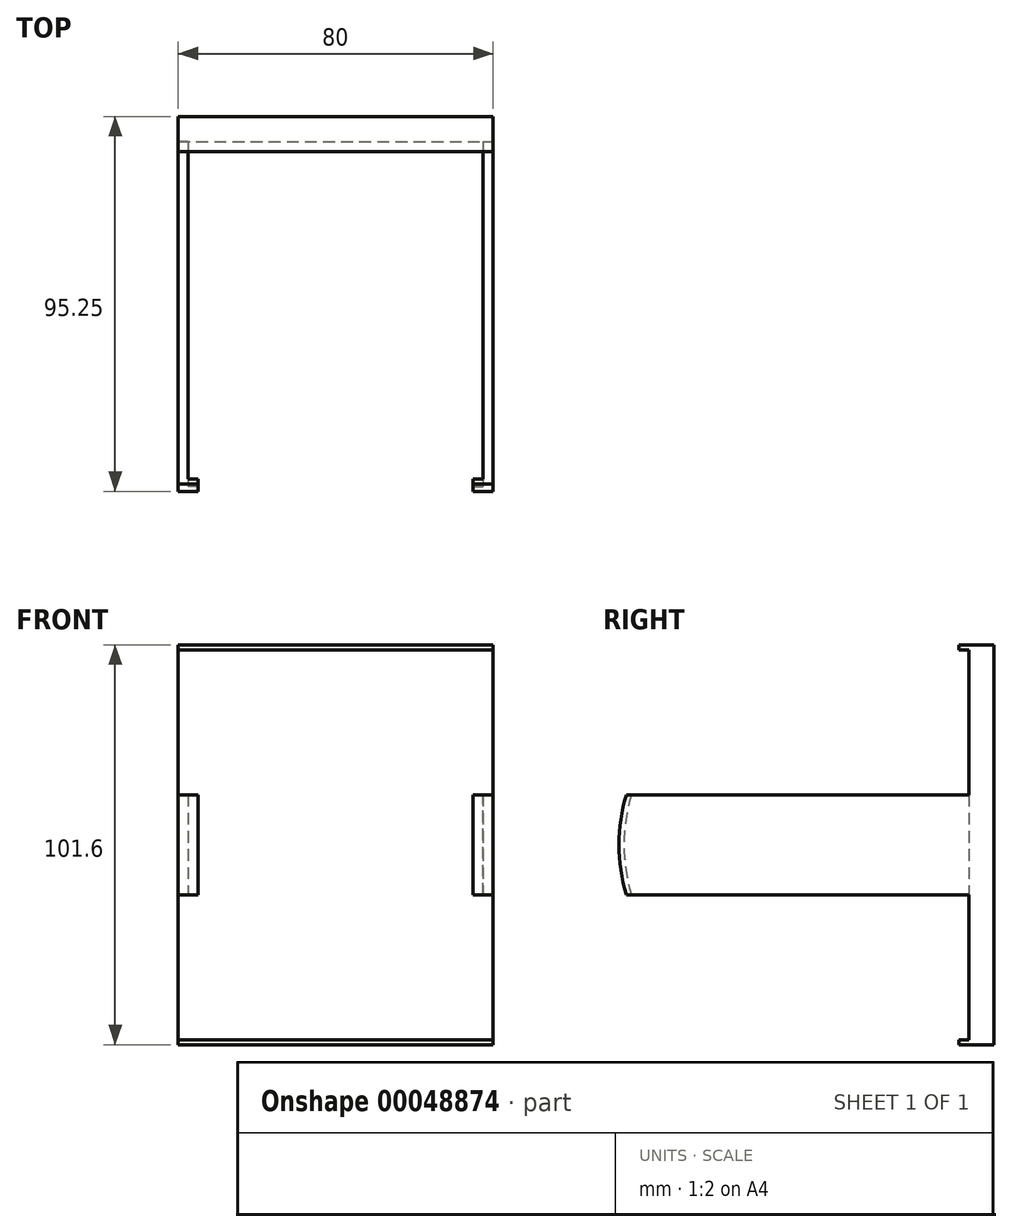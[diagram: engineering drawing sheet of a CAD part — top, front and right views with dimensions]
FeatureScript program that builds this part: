
annotation { "Feature Type Name" : "Feature", "Feature Type Description" : "" }
export const myFeature = defineFeature(function(context is Context, id is Id, definition is map)
    precondition{}
    {
        {
            var Q0;
            Q0=qCreatedBy(makeId("Front.planeOp"),FACE);
            var sketch = newSketch(context, id + "F0", { "sketchPlane" : qUnion([Q0])});
            skLineSegment(sketch, "E0.bottom", {"start": v(-21.88, 20.93) * mm, "end": v(58.12, 20.93) * mm});
            skLineSegment(sketch, "E0.top", {"start": v(-21.88, -80.67) * mm, "end": v(58.12, -80.67) * mm});
            skLineSegment(sketch, "E0.left", {"start": v(-21.88, 20.93) * mm, "end": v(-21.88, -80.67) * mm});
            skLineSegment(sketch, "E0.right", {"start": v(58.12, 20.93) * mm, "end": v(58.12, -80.67) * mm});
            skSolve(sketch);
        }
        {
            var Q0;
            Q0=makeQuery(id+"F0.imprint","IMPRINT",FACE,{"disambiguationData":[TD([[makeQuery(id+"F0.imprint","IMPRINT",EDGE,{"derivedFrom":sQuery(id+"F0.wireOp",EDGE,"E0.bottom")}),-1.0]])]});
            extrude(context, id + "F1", {"entities" : qUnion([Q0]), "depth" : 6.35 * mm});
        }
        {
            var Q0;
            Q0=makeQuery(id+"F1.opExtrude","SWEPT_FACE",FACE,{"disambiguationData":[OSD([sQuery(id+"F0.wireOp",EDGE,"E0.right")])]});
            var sketch = newSketch(context, id + "F2", { "sketchPlane" : qUnion([Q0])});
            skPoint(sketch, "E1", {"position": v(-50.8, -29.87) * mm});
            skLineSegment(sketch, "E2", {"start": v(-6.35, -42.57) * mm, "end": v(-6.35, -29.87) * mm});
            skLineSegment(sketch, "E3", {"start": v(-6.35, -29.87) * mm, "end": v(-6.35, -17.17) * mm});
            skLineSegment(sketch, "E4", {"start": v(-6.35, -42.57) * mm, "end": v(-93.4, -42.57) * mm});
            skLineSegment(sketch, "E5", {"start": v(-6.35, -17.17) * mm, "end": v(-93.4, -17.17) * mm});
            skArc(sketch, "E6.trimOffspring", {"start": v(-93.4, -17.17) * mm, "mid": v(-95.25, -29.87) * mm, "end": v(-93.4, -42.57) * mm});
            skPoint(sketch, "E7.orphan", {"position": v(-50.8, 14.58) * mm});
            skPoint(sketch, "E8.orphan", {"position": v(-95.25, -29.87) * mm});
            skPoint(sketch, "E9.orphan", {"position": v(-50.8, -74.32) * mm});
            skSolve(sketch);
        }
        {
            var Q0;
            Q0=makeQuery(id+"F2.imprint","IMPRINT",FACE,{"disambiguationData":[TD([[makeQuery(id+"F2.imprint","IMPRINT",EDGE,{"derivedFrom":sQuery(id+"F2.wireOp",EDGE,"E2")}),-1.0]])]});
            extrude(context, id + "F3", {"entities" : qUnion([Q0]), "operationType" : NewBodyOperationType.ADD, "oppositeDirection" : true, "depth" : 2.54 * mm});
        }
        {
            var Q0;
            Q0=makeQuery(id+"F1.opExtrude","SWEPT_FACE",FACE,{"disambiguationData":[OSD([sQuery(id+"F0.wireOp",EDGE,"E0.left")])]});
            var sketch = newSketch(context, id + "F4", { "sketchPlane" : qUnion([Q0])});
            skLineSegment(sketch, "E10", {"start": v(6.35, -29.87) * mm, "end": v(95.25, -29.87) * mm, "construction": true});
            skPoint(sketch, "E10.endSnap0", {"position": v(6.35, -29.87) * mm});
            skLineSegment(sketch, "E11", {"start": v(6.35, -42.57) * mm, "end": v(6.35, -29.87) * mm, "construction": true});
            skLineSegment(sketch, "E12", {"start": v(6.35, -29.87) * mm, "end": v(6.35, -17.17) * mm, "construction": true});
            skLineSegment(sketch, "E13", {"start": v(6.35, -17.17) * mm, "end": v(93.4, -17.17) * mm});
            skLineSegment(sketch, "E14", {"start": v(6.35, -42.57) * mm, "end": v(93.4, -42.57) * mm});
            skArc(sketch, "E15.trimOffspring", {"start": v(93.4, -42.57) * mm, "mid": v(95.25, -29.87) * mm, "end": v(93.4, -17.17) * mm});
            skSolve(sketch);
        }
        {
            var Q0;
            {var subQ2=sQuery(id+"F4.wireOp",EDGE,"E13");Q0=makeQuery(id+"F4.imprint","IMPRINT",FACE,{"disambiguationData":[TD([[makeQuery(id+"F4.imprint","IMPRINT",EDGE,{"derivedFrom":subQ2}),-1.0]])]});}
            extrude(context, id + "F5", {"entities" : qUnion([Q0]), "operationType" : NewBodyOperationType.ADD, "oppositeDirection" : true, "depth" : 2.54 * mm});
        }
        {
            var Q0;
            Q0=makeQuery(id+"F5.opExtrude","CAP_FACE",FACE,{"disambiguationData":[OSD([sQuery(id+"F0.wireOp",EDGE,"E0.left"),sQuery(id+"F4.wireOp",EDGE,"E13"),sQuery(id+"F4.wireOp",EDGE,"E14"),sQuery(id+"F4.wireOp",EDGE,"E15.trimOffspring")])],"isStart":false});
            var sketch = newSketch(context, id + "F6", { "sketchPlane" : qUnion([Q0])});
            skLineSegment(sketch, "E16", {"start": v(-93.4, -42.57) * mm, "end": v(-92.13, -42.57) * mm});
            skLineSegment(sketch, "E17", {"start": v(-93.4, -17.17) * mm, "end": v(-92.13, -17.17) * mm});
            skLineSegment(sketch, "E18", {"start": v(-95.25, -29.87) * mm, "end": v(-93.98, -29.87) * mm});
            skArc(sketch, "E19", {"start": v(-92.14, -17.17) * mm, "mid": v(-93.98, -29.87) * mm, "end": v(-92.14, -42.57) * mm});
            skPoint(sketch, "E20.orphan", {"position": v(-92.13, -29.87) * mm});
            skPoint(sketch, "E21.end.orphan", {"position": v(-6.35, -29.87) * mm});
            skSolve(sketch);
        }
        {
            var Q0;
            {var subQ3=sQuery(id+"F6.wireOp",EDGE,"E18");Q0=makeQuery(id+"F6.imprint","IMPRINT",FACE,{"disambiguationData":[TD([[makeQuery(id+"F6.imprint","IMPRINT",EDGE,{"derivedFrom":subQ3}),-1.0]])]});}
            var Q1;
            {var subQ3=sQuery(id+"F6.wireOp",EDGE,"E18");Q1=makeQuery(id+"F6.imprint","IMPRINT",FACE,{"disambiguationData":[TD([[makeQuery(id+"F6.imprint","IMPRINT",EDGE,{"derivedFrom":subQ3}),1.0]])]});}
            extrude(context, id + "F7", {"entities" : qUnion([Q0, Q1]), "operationType" : NewBodyOperationType.ADD, "depth" : 2.54 * mm});
        }
        {
            var Q0;
            Q0=makeQuery(id+"F3.opExtrude","CAP_FACE",FACE,{"disambiguationData":[OSD([sQuery(id+"F2.wireOp",EDGE,"E2"),sQuery(id+"F2.wireOp",EDGE,"E3"),sQuery(id+"F2.wireOp",EDGE,"E4"),sQuery(id+"F2.wireOp",EDGE,"E5"),sQuery(id+"F2.wireOp",EDGE,"E6.trimOffspring")])],"isStart":false});
            var sketch = newSketch(context, id + "F8", { "sketchPlane" : qUnion([Q0])});
            skLineSegment(sketch, "E22", {"start": v(95.25, -29.87) * mm, "end": v(93.98, -29.87) * mm});
            skLineSegment(sketch, "E23", {"start": v(93.4, -17.17) * mm, "end": v(92.13, -17.17) * mm});
            skLineSegment(sketch, "E24", {"start": v(93.4, -42.57) * mm, "end": v(92.13, -42.57) * mm});
            skLineSegment(sketch, "E25", {"start": v(93.98, -29.87) * mm, "end": v(6.35, -29.87) * mm});
            skArc(sketch, "E26", {"start": v(92.13, -42.57) * mm, "mid": v(94, -29.87) * mm, "end": v(92.13, -17.17) * mm});
            skSolve(sketch);
        }
        {
            var Q0;
            {var subQ3=sQuery(id+"F8.wireOp",EDGE,"E23");Q0=makeQuery(id+"F8.imprint","IMPRINT",FACE,{"disambiguationData":[TD([[makeQuery(id+"F8.imprint","IMPRINT",EDGE,{"derivedFrom":subQ3}),-1.0]])]});}
            var Q1;
            {var subQ3=sQuery(id+"F8.wireOp",EDGE,"E24");Q1=makeQuery(id+"F8.imprint","IMPRINT",FACE,{"disambiguationData":[TD([[makeQuery(id+"F8.imprint","IMPRINT",EDGE,{"derivedFrom":subQ3}),1.0]])]});}
            extrude(context, id + "F9", {"entities" : qUnion([Q0, Q1]), "operationType" : NewBodyOperationType.ADD, "depth" : 2.54 * mm});
        }
        {
            var Q0;
            Q0=makeQuery(id+"F1.opExtrude","CAP_FACE",FACE,{"disambiguationData":[OSD([sQuery(id+"F0.wireOp",EDGE,"E0.bottom"),sQuery(id+"F0.wireOp",EDGE,"E0.top"),sQuery(id+"F0.wireOp",EDGE,"E0.left"),sQuery(id+"F0.wireOp",EDGE,"E0.right")])],"isStart":false});
            var sketch = newSketch(context, id + "F10", { "sketchPlane" : qUnion([Q0])});
            skLineSegment(sketch, "E27.bottom", {"start": v(-21.88, 20.93) * mm, "end": v(58.12, 20.93) * mm});
            skLineSegment(sketch, "E27.top", {"start": v(-21.88, 19.66) * mm, "end": v(58.12, 19.66) * mm});
            skLineSegment(sketch, "E27.left", {"start": v(-21.88, 20.93) * mm, "end": v(-21.88, 19.66) * mm});
            skLineSegment(sketch, "E27.right", {"start": v(58.12, 20.93) * mm, "end": v(58.12, 19.66) * mm});
            skLineSegment(sketch, "E28.bottom", {"start": v(-21.88, -80.67) * mm, "end": v(58.12, -80.67) * mm});
            skLineSegment(sketch, "E28.top", {"start": v(-21.88, -79.4) * mm, "end": v(58.12, -79.4) * mm});
            skLineSegment(sketch, "E28.left", {"start": v(-21.88, -80.67) * mm, "end": v(-21.88, -79.4) * mm});
            skLineSegment(sketch, "E28.right", {"start": v(58.12, -80.67) * mm, "end": v(58.12, -79.4) * mm});
            skSolve(sketch);
        }
        {
            var Q0;
            Q0=makeQuery(id+"F10.imprint","IMPRINT",FACE,{"disambiguationData":[TD([[makeQuery(id+"F10.imprint","IMPRINT",EDGE,{"derivedFrom":sQuery(id+"F10.wireOp",EDGE,"E27.bottom")}),-1.0]])]});
            extrude(context, id + "F11", {"entities" : qUnion([Q0]), "operationType" : NewBodyOperationType.ADD, "depth" : 2.54 * mm});
        }
        {
            var Q0;
            Q0=makeQuery(id+"F10.imprint","IMPRINT",FACE,{"disambiguationData":[TD([[makeQuery(id+"F10.imprint","IMPRINT",EDGE,{"derivedFrom":sQuery(id+"F10.wireOp",EDGE,"E28.bottom")}),1.0]])]});
            extrude(context, id + "F12", {"entities" : qUnion([Q0]), "operationType" : NewBodyOperationType.ADD, "depth" : 2.54 * mm});
        }
    });
